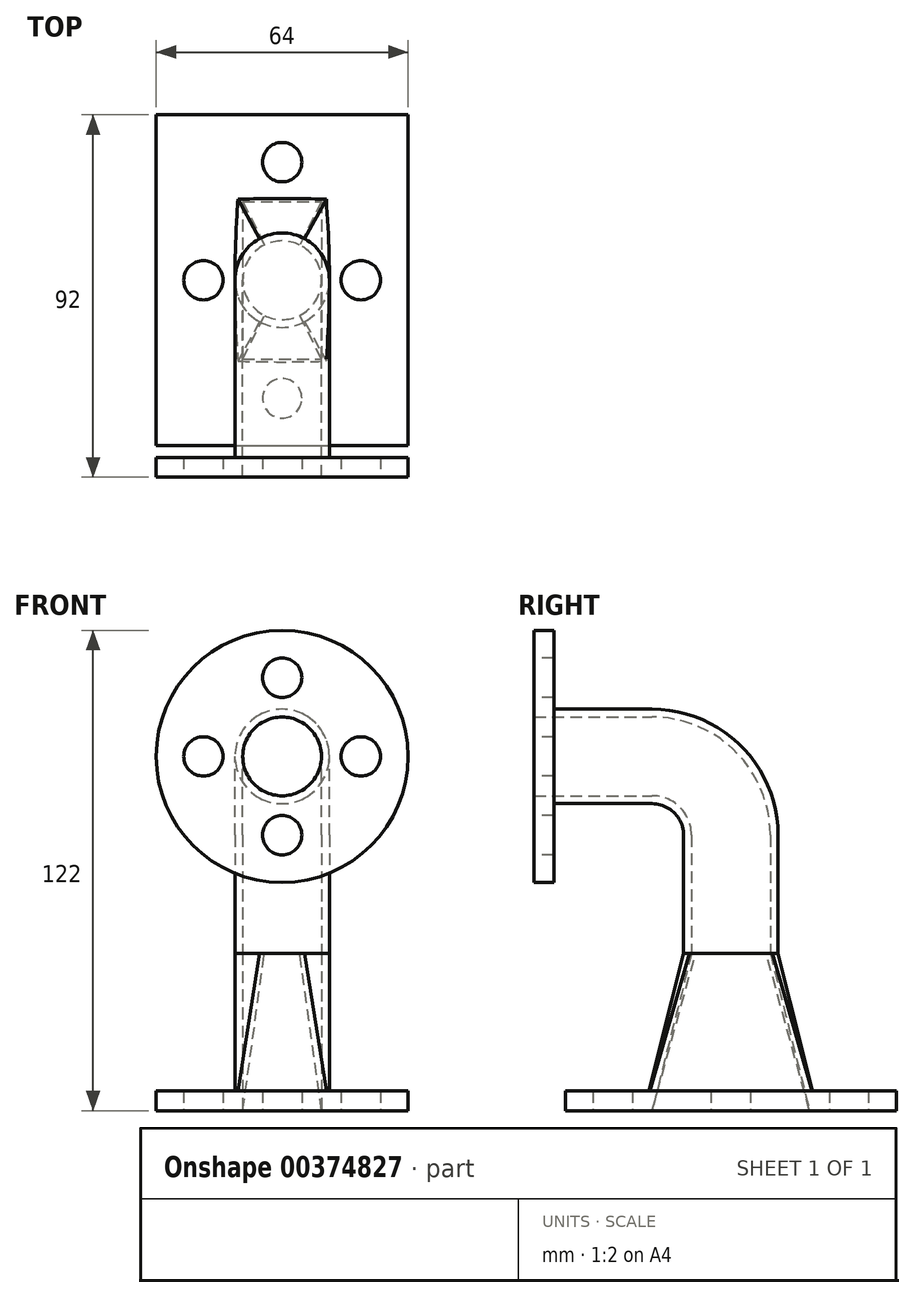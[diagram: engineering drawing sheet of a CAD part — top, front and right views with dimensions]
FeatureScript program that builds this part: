
annotation { "Feature Type Name" : "Feature", "Feature Type Description" : "" }
export const myFeature = defineFeature(function(context is Context, id is Id, definition is map)
    precondition{}
    {
        {
            var Q0;
            Q0=qCreatedBy(makeId("Top.planeOp"),FACE);
            var sketch = newSketch(context, id + "F0", { "sketchPlane" : qUnion([Q0])});
            skLineSegment(sketch, "E0.bottom", {"start": v(12, 22) * mm, "end": v(-12, 22) * mm});
            skLineSegment(sketch, "E0.top", {"start": v(12, -22) * mm, "end": v(-12, -22) * mm});
            skLineSegment(sketch, "E0.left", {"start": v(12, 22) * mm, "end": v(12, -22) * mm});
            skLineSegment(sketch, "E0.right", {"start": v(-12, 22) * mm, "end": v(-12, -22) * mm});
            skPoint(sketch, "E0.middle", {"position": v(0, 0) * mm});
            skSolve(sketch);
        }
        {
            var Q0;
            Q0=qCreatedBy(makeId("Top.planeOp"),FACE);
            cPlane(context, id + "F1", {"entities" : qUnion([Q0]), "cplaneType" : CPlaneType.OFFSET, "offset" : 40 * mm, "width" : 150 * mm, "height" : 150 * mm});
        }
        {
            var Q0;
            Q0=qCreatedBy(id+"F1.planeOp",FACE);
            var sketch = newSketch(context, id + "F2", { "sketchPlane" : qUnion([Q0])});
            skPoint(sketch, "E1.middle", {"position": v(0, 0) * mm});
            skArc(sketch, "E2", {"start": v(5.75, 10.53) * mm, "mid": v(0, 12) * mm, "end": v(-5.75, 10.53) * mm});
            skArc(sketch, "E3", {"start": v(-5.75, 10.53) * mm, "mid": v(-12, 0) * mm, "end": v(-5.75, -10.53) * mm});
            skArc(sketch, "E4", {"start": v(-5.75, -10.53) * mm, "mid": v(0, -12) * mm, "end": v(5.75, -10.53) * mm});
            skArc(sketch, "E5", {"start": v(5.75, -10.53) * mm, "mid": v(12, 0) * mm, "end": v(5.75, 10.53) * mm});
            skPoint(sketch, "E1.bottom.end.orphan", {"position": v(-12, 22) * mm});
            skPoint(sketch, "E6.orphan", {"position": v(12, 22) * mm});
            skPoint(sketch, "E1.top.start.orphan", {"position": v(12, -22) * mm});
            skPoint(sketch, "E1.right.end.orphan", {"position": v(-12, -22) * mm});
            skSolve(sketch);
        }
        {
            var Q0;
            Q0=makeQuery(id+"F2.imprint","IMPRINT",FACE,{"disambiguationData":[TD([[makeQuery(id+"F2.imprint","IMPRINT",EDGE,{"derivedFrom":sQuery(id+"F2.wireOp",EDGE,"E2")}),1.0]])]});
            var Q1;
            Q1=makeQuery(id+"F0.imprint","IMPRINT",FACE,{"disambiguationData":[TD([[makeQuery(id+"F0.imprint","IMPRINT",EDGE,{"derivedFrom":sQuery(id+"F0.wireOp",EDGE,"E0.bottom")}),1.0]])]});
            loft(context, id + "F3", {"sheetProfilesArray" : [{ "sheetProfileEntities" : qUnion([Q0]) }, { "sheetProfileEntities" : qUnion([Q1]) }]});
        }
        {
            var Q0;
            Q0=makeQuery(id+"F3.opLoft","CAP_FACE",FACE,{"disambiguationData":[OSD([makeQuery(id+"F0.imprint","IMPRINT",FACE,{"disambiguationData":[TD([[makeQuery(id+"F0.imprint","IMPRINT",EDGE,{"derivedFrom":sQuery(id+"F0.wireOp",EDGE,"E0.bottom")}),1.0]])]})])],"isStart":true});
            var sketch = newSketch(context, id + "F4", { "sketchPlane" : qUnion([Q0])});
            skLineSegment(sketch, "E7.bottom", {"start": v(-10, -20) * mm, "end": v(10, -20) * mm});
            skLineSegment(sketch, "E7.top", {"start": v(-10, 20) * mm, "end": v(10, 20) * mm});
            skLineSegment(sketch, "E7.left", {"start": v(-10, -20) * mm, "end": v(-10, 20) * mm});
            skLineSegment(sketch, "E7.right", {"start": v(10, -20) * mm, "end": v(10, 20) * mm});
            skPoint(sketch, "E7.middle", {"position": v(0, 0) * mm});
            skSolve(sketch);
        }
        {
            var Q0;
            Q0=makeQuery(id+"F3.opLoft","CAP_FACE",FACE,{"disambiguationData":[OSD([makeQuery(id+"F2.imprint","IMPRINT",FACE,{"disambiguationData":[TD([[makeQuery(id+"F2.imprint","IMPRINT",EDGE,{"derivedFrom":sQuery(id+"F2.wireOp",EDGE,"E2")}),1.0]])]})])],"isStart":true});
            var sketch = newSketch(context, id + "F5", { "sketchPlane" : qUnion([Q0])});
            skPoint(sketch, "E8.middle", {"position": v(0, 0) * mm});
            skArc(sketch, "E9", {"start": v(4.47, 8.94) * mm, "mid": v(0, 10) * mm, "end": v(-4.47, 8.94) * mm});
            skArc(sketch, "E10", {"start": v(-4.47, 8.94) * mm, "mid": v(-10, 0) * mm, "end": v(-4.47, -8.94) * mm});
            skArc(sketch, "E11", {"start": v(-4.47, -8.94) * mm, "mid": v(0, -10) * mm, "end": v(4.47, -8.94) * mm});
            skArc(sketch, "E12", {"start": v(4.47, -8.94) * mm, "mid": v(10, 0) * mm, "end": v(4.47, 8.94) * mm});
            skPoint(sketch, "E13.orphan", {"position": v(-10, -20) * mm});
            skPoint(sketch, "E8.bottom.end.orphan", {"position": v(-10, 20) * mm});
            skPoint(sketch, "E14.orphan", {"position": v(10, 20) * mm});
            skPoint(sketch, "E8.left.end.orphan", {"position": v(10, -20) * mm});
            skSolve(sketch);
        }
        {
            var Q0;
            Q0=makeQuery(id+"F4.imprint","IMPRINT",FACE,{"disambiguationData":[TD([[makeQuery(id+"F4.imprint","IMPRINT",EDGE,{"derivedFrom":sQuery(id+"F4.wireOp",EDGE,"E7.bottom")}),1.0]])]});
            var sketch = newSketch(context, id + "F6", { "sketchPlane" : qUnion([Q0])});
            skLineSegment(sketch, "E15.bottom", {"start": v(-32, -42) * mm, "end": v(32, -42) * mm});
            skLineSegment(sketch, "E15.top", {"start": v(-32, 42) * mm, "end": v(32, 42) * mm});
            skLineSegment(sketch, "E15.left", {"start": v(-32, -42) * mm, "end": v(-32, 42) * mm});
            skLineSegment(sketch, "E15.right", {"start": v(32, -42) * mm, "end": v(32, 42) * mm});
            skPoint(sketch, "E15.middle", {"position": v(0, 0) * mm});
            skSolve(sketch);
        }
        {
            var Q0;
            Q0 = qSketchRegion(id + "F6", true);
            extrude(context, id + "F7", {"entities" : qUnion([Q0]), "operationType" : NewBodyOperationType.ADD, "oppositeDirection" : true, "depth" : 5 * mm});
        }
        {
            var Q1;
            Q1=makeQuery(id+"F4.imprint","IMPRINT",FACE,{"disambiguationData":[TD([[makeQuery(id+"F4.imprint","IMPRINT",EDGE,{"derivedFrom":sQuery(id+"F4.wireOp",EDGE,"E7.bottom")}),1.0]])]});
            var Q2;
            Q2=makeQuery(id+"F5.imprint","IMPRINT",FACE,{"disambiguationData":[TD([[makeQuery(id+"F5.imprint","IMPRINT",EDGE,{"derivedFrom":sQuery(id+"F5.wireOp",EDGE,"E9")}),1.0]])]});
            loft(context, id + "F8", {"operationType" : NewBodyOperationType.REMOVE, "sheetProfilesArray" : [{ "sheetProfileEntities" : qUnion([Q1]) }, { "sheetProfileEntities" : qUnion([Q2]) }]});
        }
        {
            var Q0;
            Q0=makeQuery(id+"F7.boolean.opBoolean","MERGE",FACE,{"derivedFrom":[makeQuery(id+"F3.opLoft","CAP_FACE",FACE,{"disambiguationData":[OSD([makeQuery(id+"F0.imprint","IMPRINT",FACE,{"disambiguationData":[TD([[makeQuery(id+"F0.imprint","IMPRINT",EDGE,{"derivedFrom":sQuery(id+"F0.wireOp",EDGE,"E0.bottom")}),1.0]])]})])],"isStart":true}),makeQuery(id+"F7.opExtrude","CAP_FACE",FACE,{"disambiguationData":[OSD([sQuery(id+"F6.wireOp",EDGE,"E15.bottom"),sQuery(id+"F6.wireOp",EDGE,"E15.top"),sQuery(id+"F6.wireOp",EDGE,"E15.left"),sQuery(id+"F6.wireOp",EDGE,"E15.right")])],"isStart":true})]});
            var sketch = newSketch(context, id + "F9", { "sketchPlane" : qUnion([Q0])});
            skCircle(sketch, "E16", {"center": v(0, -30) * mm, "radius": 5 * mm});
            skCircle(sketch, "E17", {"center": v(0, 30) * mm, "radius": 5 * mm});
            skCircle(sketch, "E18", {"center": v(-20, 0) * mm, "radius": 5 * mm});
            skCircle(sketch, "E19", {"center": v(20, 0) * mm, "radius": 5 * mm});
            skSolve(sketch);
        }
        {
            var Q0;
            Q0=makeQuery(id+"F9.imprint","IMPRINT",FACE,{"disambiguationData":[TD([[makeQuery(id+"F9.imprint","IMPRINT",EDGE,{"derivedFrom":sQuery(id+"F9.wireOp",EDGE,"E16")}),1.0]])]});
            var Q1;
            Q1=makeQuery(id+"F9.imprint","IMPRINT",FACE,{"disambiguationData":[TD([[makeQuery(id+"F9.imprint","IMPRINT",EDGE,{"derivedFrom":sQuery(id+"F9.wireOp",EDGE,"E18")}),1.0]])]});
            var Q2;
            Q2=makeQuery(id+"F9.imprint","IMPRINT",FACE,{"disambiguationData":[TD([[makeQuery(id+"F9.imprint","IMPRINT",EDGE,{"derivedFrom":sQuery(id+"F9.wireOp",EDGE,"E17")}),1.0]])]});
            var Q3;
            Q3=makeQuery(id+"F9.imprint","IMPRINT",FACE,{"disambiguationData":[TD([[makeQuery(id+"F9.imprint","IMPRINT",EDGE,{"derivedFrom":sQuery(id+"F9.wireOp",EDGE,"E19")}),1.0]])]});
            var Q4;
            Q4=makeQuery(id+"F7.opExtrude","CAP_FACE",FACE,{"disambiguationData":[OSD([sQuery(id+"F6.wireOp",EDGE,"E15.bottom"),sQuery(id+"F6.wireOp",EDGE,"E15.top"),sQuery(id+"F6.wireOp",EDGE,"E15.left"),sQuery(id+"F6.wireOp",EDGE,"E15.right")])],"isStart":false});
            extrude(context, id + "F10", {"entities" : qUnion([Q0, Q1, Q2, Q3]), "operationType" : NewBodyOperationType.REMOVE, "endBound" : BoundingType.UP_TO_SURFACE, "oppositeDirection" : true, "endBoundEntityFace" : qUnion([Q4]), "depth" : 25 * mm});
        }
        {
            var Q0;
            Q0=makeQuery(id+"F3.opLoft","CAP_FACE",FACE,{"disambiguationData":[OSD([makeQuery(id+"F2.imprint","IMPRINT",FACE,{"disambiguationData":[TD([[makeQuery(id+"F2.imprint","IMPRINT",EDGE,{"derivedFrom":sQuery(id+"F2.wireOp",EDGE,"E2")}),1.0]])]})])],"isStart":true});
            extrude(context, id + "F11", {"entities" : qUnion([Q0]), "operationType" : NewBodyOperationType.ADD, "depth" : 30 * mm});
        }
        {
            var Q0;
            Q0=qCreatedBy(makeId("Right.planeOp"),FACE);
            var sketch = newSketch(context, id + "F12", { "sketchPlane" : qUnion([Q0])});
            skLineSegment(sketch, "E20", {"start": v(0, 70) * mm, "end": v(-20, 70) * mm});
            skArc(sketch, "E21", {"start": v(0, 70) * mm, "mid": v(-5.86, 84.14) * mm, "end": v(-20, 90) * mm});
            skSolve(sketch);
        }
        {
            var Q0;
            Q0=makeQuery(id+"F11.opExtrude","CAP_FACE",FACE,{"disambiguationData":[OSD([makeQuery(id+"F2.imprint","IMPRINT",FACE,{"disambiguationData":[TD([[makeQuery(id+"F2.imprint","IMPRINT",EDGE,{"derivedFrom":sQuery(id+"F2.wireOp",EDGE,"E2")}),1.0]])]})])],"isStart":false});
            var Q1;
            Q1=sQuery(id+"F12.wireOp",EDGE,"E21");
            sweep(context, id + "F13", {"operationType" : NewBodyOperationType.ADD, "profiles" : qUnion([Q0]), "path" : qUnion([Q1])});
        }
        {
            var Q0;
            Q0=makeQuery(id+"F13.opSweep","CAP_FACE",FACE,{"disambiguationData":[OSD([makeQuery(id+"F2.imprint","IMPRINT",FACE,{"disambiguationData":[TD([[makeQuery(id+"F2.imprint","IMPRINT",EDGE,{"derivedFrom":sQuery(id+"F2.wireOp",EDGE,"E2")}),1.0]])]}),sQuery(id+"F12.wireOp",VERTEX,"E21.end")])],"isStart":false});
            extrude(context, id + "F14", {"entities" : qUnion([Q0]), "operationType" : NewBodyOperationType.ADD, "depth" : 30 * mm});
        }
        {
            var Q0;
            Q0=makeQuery(id+"F14.opExtrude","CAP_FACE",FACE,{"disambiguationData":[OSD([makeQuery(id+"F2.imprint","IMPRINT",FACE,{"disambiguationData":[TD([[makeQuery(id+"F2.imprint","IMPRINT",EDGE,{"derivedFrom":sQuery(id+"F2.wireOp",EDGE,"E2")}),1.0]])]}),sQuery(id+"F12.wireOp",VERTEX,"E21.end")])],"isStart":false});
            var sketch = newSketch(context, id + "F15", { "sketchPlane" : qUnion([Q0])});
            skCircle(sketch, "E22", {"center": v(0, 90) * mm, "radius": 32 * mm});
            skSolve(sketch);
        }
        {
            var Q0;
            Q0=makeQuery(id+"F15.imprint","IMPRINT",FACE,{"disambiguationData":[TD([[makeQuery(id+"F15.imprint","IMPRINT",EDGE,{"derivedFrom":sQuery(id+"F15.wireOp",EDGE,"E22")}),1.0]])]});
            extrude(context, id + "F16", {"entities" : qUnion([Q0]), "operationType" : NewBodyOperationType.ADD, "oppositeDirection" : true, "depth" : 5 * mm});
        }
        {
            var Q0;
            {var subQ0=sQuery(id+"F12.wireOp",VERTEX,"E21.end");var subQ1=sQuery(id+"F2.wireOp",EDGE,"E5");var subQ2=sQuery(id+"F2.wireOp",EDGE,"E4");var subQ3=sQuery(id+"F2.wireOp",EDGE,"E3");var subQ4=sQuery(id+"F2.wireOp",EDGE,"E2");Q0=makeQuery(id+"F16.boolean.opBoolean","MERGE",FACE,{"derivedFrom":[makeQuery(id+"F14.opExtrude","CAP_FACE",FACE,{"disambiguationData":[OSD([makeQuery(id+"F2.imprint","IMPRINT",FACE,{"disambiguationData":[TD([[makeQuery(id+"F2.imprint","IMPRINT",EDGE,{"derivedFrom":subQ4}),1.0]])]}),subQ0])],"isStart":false}),makeQuery(id+"F16.opExtrude","CAP_FACE",FACE,{"disambiguationData":[OSD([subQ4,subQ3,subQ2,subQ1,subQ0,sQuery(id+"F15.wireOp",EDGE,"E22")])],"isStart":true})]});}
            var sketch = newSketch(context, id + "F17", { "sketchPlane" : qUnion([Q0])});
            skLineSegment(sketch, "E23", {"start": v(0, 0) * mm, "end": v(0, 90) * mm});
            skCircle(sketch, "E24", {"center": v(0, 110) * mm, "radius": 5 * mm});
            skCircle(sketch, "E25.1.0", {"center": v(-20, 90) * mm, "radius": 5 * mm});
            skCircle(sketch, "E25.2.0", {"center": v(0, 70) * mm, "radius": 5 * mm});
            skPoint(sketch, "E25.center", {"position": v(0, 90) * mm});
            skCircle(sketch, "E26.1.3.0", {"center": v(20, 90) * mm, "radius": 5 * mm});
            skSolve(sketch);
        }
        {
            var Q0;
            Q0=makeQuery(id+"F17.imprint","IMPRINT",FACE,{"disambiguationData":[TD([[makeQuery(id+"F17.imprint","IMPRINT",EDGE,{"derivedFrom":sQuery(id+"F17.wireOp",EDGE,"E26.1.3.0")}),1.0]])]});
            var Q1;
            {var subQ0=sQuery(id+"F17.wireOp",EDGE,"E25.2.0");var subQ1=sQuery(id+"F17.wireOp",EDGE,"E23");var subQ2=makeQuery(id+"F17.imprint","INTERSECT",VERTEX,{"disambiguationData":[OD(0.0)],"derivedFrom":[subQ1,subQ0]});Q1=makeQuery(id+"F17.imprint","IMPRINT",FACE,{"disambiguationData":[TD([[makeQuery(id+"F17.imprint","IMPRINT",EDGE,{"disambiguationData":[TD([[subQ2,-1.0]])],"derivedFrom":subQ1}),1.0]])]});}
            var Q2;
            {var subQ0=sQuery(id+"F17.wireOp",EDGE,"E25.2.0");var subQ1=sQuery(id+"F17.wireOp",EDGE,"E23");var subQ2=makeQuery(id+"F17.imprint","INTERSECT",VERTEX,{"disambiguationData":[OD(0.0)],"derivedFrom":[subQ1,subQ0]});Q2=makeQuery(id+"F17.imprint","IMPRINT",FACE,{"disambiguationData":[TD([[makeQuery(id+"F17.imprint","IMPRINT",EDGE,{"disambiguationData":[TD([[subQ2,-1.0]])],"derivedFrom":subQ1}),-1.0]])]});}
            var Q3;
            Q3=makeQuery(id+"F17.imprint","IMPRINT",FACE,{"disambiguationData":[TD([[makeQuery(id+"F17.imprint","IMPRINT",EDGE,{"derivedFrom":sQuery(id+"F17.wireOp",EDGE,"E25.1.0")}),1.0]])]});
            var Q4;
            Q4=makeQuery(id+"F17.imprint","IMPRINT",FACE,{"disambiguationData":[TD([[makeQuery(id+"F17.imprint","IMPRINT",EDGE,{"derivedFrom":sQuery(id+"F17.wireOp",EDGE,"E24")}),1.0]])]});
            var Q5;
            Q5=makeQuery(id+"F16.opExtrude","CAP_FACE",FACE,{"disambiguationData":[OSD([sQuery(id+"F2.wireOp",EDGE,"E2"),sQuery(id+"F2.wireOp",EDGE,"E3"),sQuery(id+"F2.wireOp",EDGE,"E4"),sQuery(id+"F2.wireOp",EDGE,"E5"),sQuery(id+"F12.wireOp",VERTEX,"E21.end"),sQuery(id+"F15.wireOp",EDGE,"E22")])],"isStart":false});
            extrude(context, id + "F18", {"entities" : qUnion([Q0, Q1, Q2, Q3, Q4]), "operationType" : NewBodyOperationType.REMOVE, "endBound" : BoundingType.UP_TO_SURFACE, "oppositeDirection" : true, "endBoundEntityFace" : qUnion([Q5]), "depth" : 25 * mm});
        }
    });
